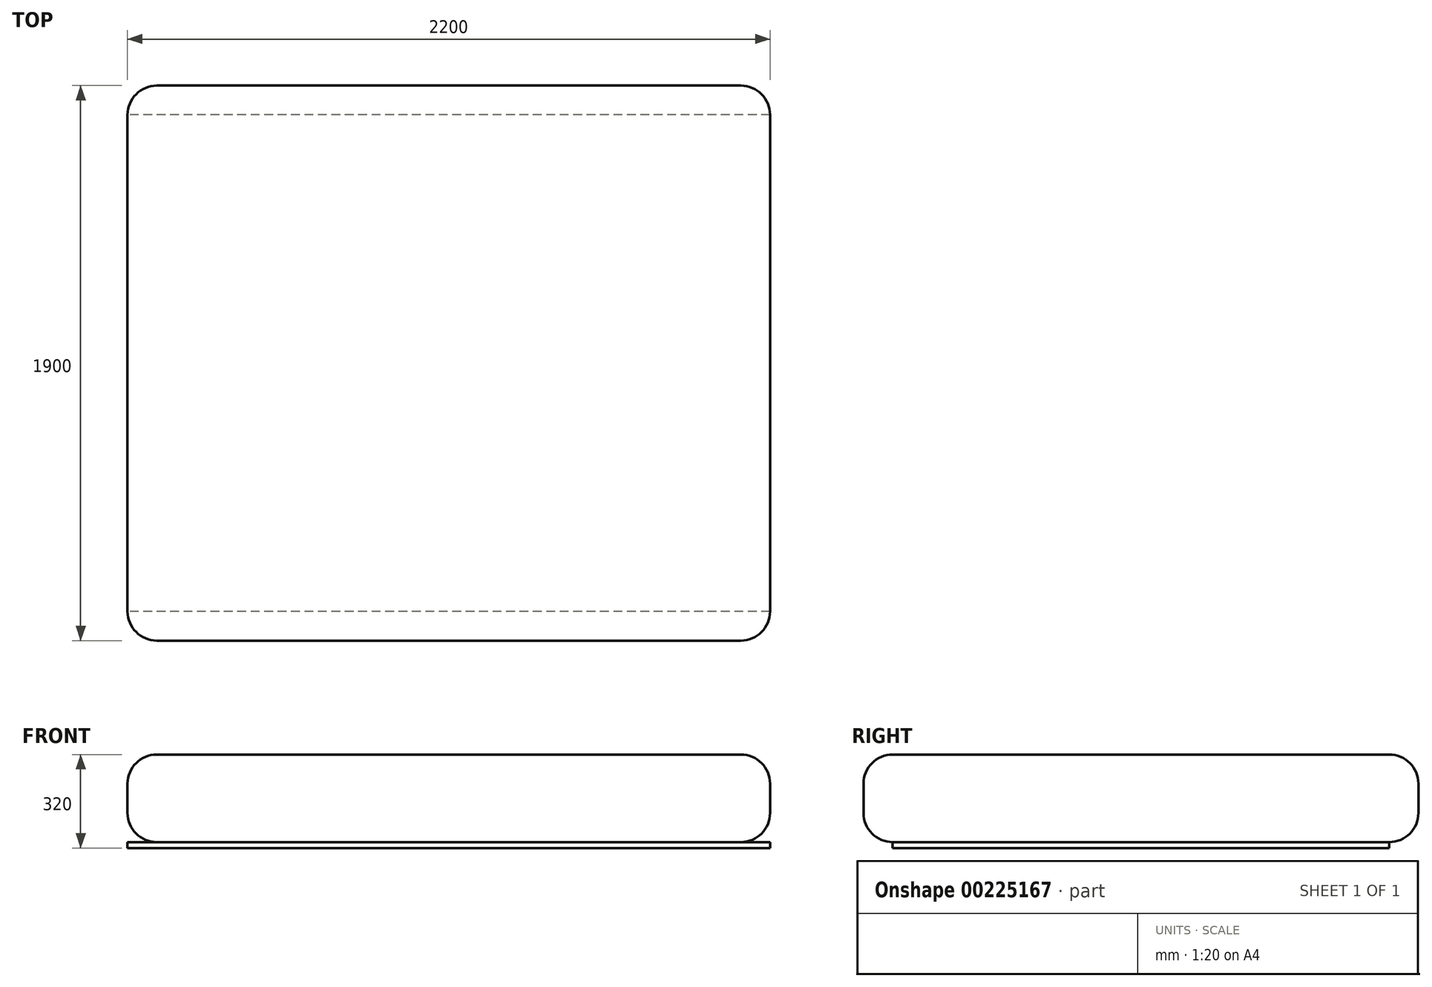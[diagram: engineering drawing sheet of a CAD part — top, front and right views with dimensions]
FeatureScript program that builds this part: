
annotation { "Feature Type Name" : "Feature", "Feature Type Description" : "" }
export const myFeature = defineFeature(function(context is Context, id is Id, definition is map)
    precondition{}
    {
        {
            var Q0;
            Q0=qCreatedBy(makeId("Top.planeOp"),FACE);
            var sketch = newSketch(context, id + "F0", { "sketchPlane" : qUnion([Q0])});
            skLineSegment(sketch, "E0.bottom", {"start": v(1100, 850) * mm, "end": v(-1100, 850) * mm});
            skLineSegment(sketch, "E0.top", {"start": v(1100, -850) * mm, "end": v(-1100, -850) * mm});
            skLineSegment(sketch, "E0.left", {"start": v(1100, 850) * mm, "end": v(1100, -850) * mm});
            skLineSegment(sketch, "E0.right", {"start": v(-1100, 850) * mm, "end": v(-1100, -850) * mm});
            skPoint(sketch, "E0.middle", {"position": v(0, 0) * mm});
            skSolve(sketch);
        }
        {
            var Q0;
            Q0 = qSketchRegion(id + "F0", true);
            extrude(context, id + "F1", {"entities" : qUnion([Q0]), "depth" : 20 * mm});
        }
        {
            var Q0;
            Q0=makeQuery(id+"F1.opExtrude","CAP_FACE",FACE,{"disambiguationData":[OSD([sQuery(id+"F0.wireOp",EDGE,"E0.bottom"),sQuery(id+"F0.wireOp",EDGE,"E0.top"),sQuery(id+"F0.wireOp",EDGE,"E0.left"),sQuery(id+"F0.wireOp",EDGE,"E0.right")])],"isStart":false});
            var sketch = newSketch(context, id + "F2", { "sketchPlane" : qUnion([Q0])});
            skLineSegment(sketch, "E1.bottom", {"start": v(1100, 950) * mm, "end": v(-1100, 950) * mm});
            skLineSegment(sketch, "E1.top", {"start": v(1100, -950) * mm, "end": v(-1100, -950) * mm});
            skLineSegment(sketch, "E1.left", {"start": v(1100, 950) * mm, "end": v(1100, -950) * mm});
            skLineSegment(sketch, "E1.right", {"start": v(-1100, 950) * mm, "end": v(-1100, -950) * mm});
            skPoint(sketch, "E1.middle", {"position": v(0, 0) * mm});
            skSolve(sketch);
        }
        {
            var Q0;
            Q0 = qSketchRegion(id + "F2", true);
            extrude(context, id + "F3", {"entities" : qUnion([Q0]), "depth" : 300 * mm});
        }
        {
            var Q0;
            Q0=makeQuery(id+"F3.opExtrude","CAP_FACE",FACE,{"disambiguationData":[OSD([sQuery(id+"F2.wireOp",EDGE,"E1.bottom"),sQuery(id+"F2.wireOp",EDGE,"E1.top"),sQuery(id+"F2.wireOp",EDGE,"E1.left"),sQuery(id+"F2.wireOp",EDGE,"E1.right")])],"isStart":false});
            var Q1;
            Q1=makeQuery(id+"F3.opExtrude","CAP_FACE",FACE,{"disambiguationData":[OSD([sQuery(id+"F2.wireOp",EDGE,"E1.bottom"),sQuery(id+"F2.wireOp",EDGE,"E1.top"),sQuery(id+"F2.wireOp",EDGE,"E1.left"),sQuery(id+"F2.wireOp",EDGE,"E1.right")])],"isStart":true});
            var Q2;
            Q2=makeQuery(id+"F3.opExtrude","SWEPT_EDGE",EDGE,{"disambiguationData":[OSD([sQuery(id+"F2.wireOp",EDGE,"E1.top"),sQuery(id+"F2.wireOp",EDGE,"E1.left")])]});
            var Q3;
            Q3=makeQuery(id+"F3.opExtrude","SWEPT_EDGE",EDGE,{"disambiguationData":[OSD([sQuery(id+"F2.wireOp",EDGE,"E1.bottom"),sQuery(id+"F2.wireOp",EDGE,"E1.left")])]});
            var Q4;
            Q4=makeQuery(id+"F3.opExtrude","SWEPT_EDGE",EDGE,{"disambiguationData":[OSD([sQuery(id+"F2.wireOp",EDGE,"E1.bottom"),sQuery(id+"F2.wireOp",EDGE,"E1.right")])]});
            var Q5;
            Q5=makeQuery(id+"F3.opExtrude","SWEPT_EDGE",EDGE,{"disambiguationData":[OSD([sQuery(id+"F2.wireOp",EDGE,"E1.top"),sQuery(id+"F2.wireOp",EDGE,"E1.right")])]});
            fillet(context, id + "F4", {"entities" : qUnion([Q0, Q1, Q2, Q3, Q4, Q5]), "radius" : 100 * mm, "tangentPropagation" : true, "allowEdgeOverflow" : false});
        }
    });
